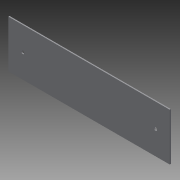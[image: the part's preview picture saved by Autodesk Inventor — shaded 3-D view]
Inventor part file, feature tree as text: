
AUTODESK INVENTOR PART (.ipt)
format: ipt  version: 2014 (Build 180170000, 170)  size: 2,140,672 bytes
history: native  units: mm
features: extrude x3, sketch x3
ambient origin geometry x8: Origin, YZ Plane, XZ Plane, XY Plane, X Axis, Y Axis, Z Axis, Center Point
bodies: Solid1 (feature_tree)
feature tree (6):
  extrude  "Extrusion1"  Depth=50.0mm
  extrude  "Extrusion2"  Depth=0.8mm TaperAngle=0.0deg
  extrude  "Extrusion3"  Depth=3.4mm
  sketch  "Sketch1"  dims[d0=170.0mm d1=50.0mm]
  sketch  "Sketch2"  dims[d2=1.2mm d3=0.0mm d4=0.8mm d5=0.0mm]
  sketch  "Sketch3"  dims[d6=3.4mm d7=3.4mm d8=15.0mm d9=15.0mm d10=0.8mm d11=0.0mm]
